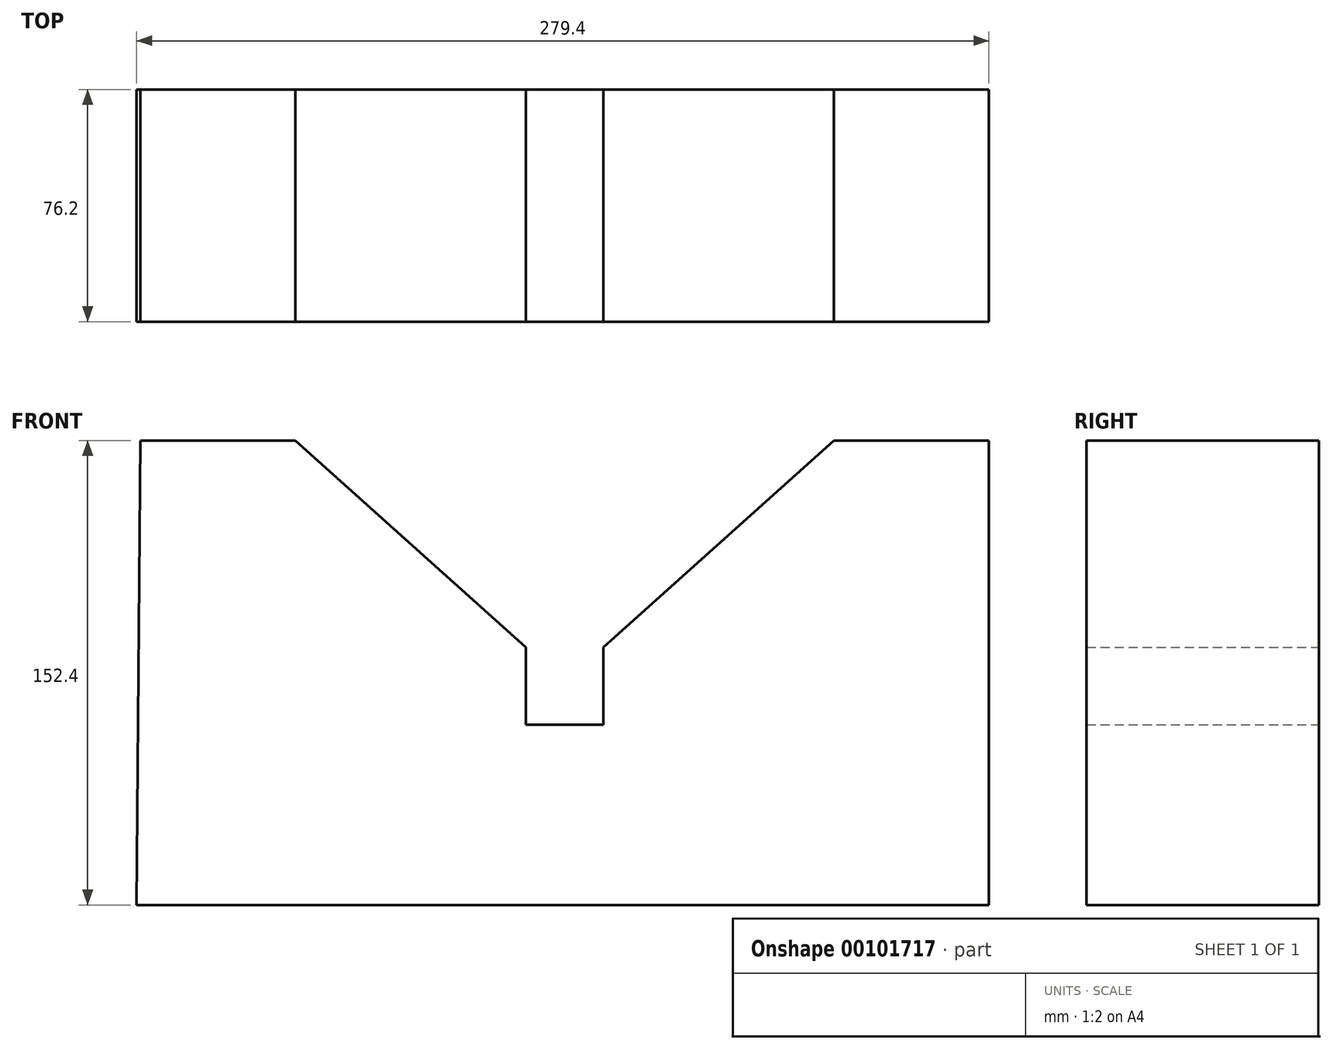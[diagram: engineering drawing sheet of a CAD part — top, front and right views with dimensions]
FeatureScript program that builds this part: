
annotation { "Feature Type Name" : "Feature", "Feature Type Description" : "" }
export const myFeature = defineFeature(function(context is Context, id is Id, definition is map)
    precondition{}
    {
        {
            var Q0;
            Q0=qCreatedBy(makeId("Front.planeOp"),FACE);
            var sketch = newSketch(context, id + "F0", { "sketchPlane" : qUnion([Q0])});
            skLineSegment(sketch, "E0", {"start": v(-116.18, 58.64) * mm, "end": v(-65.38, 58.64) * mm});
            skLineSegment(sketch, "E1", {"start": v(-65.38, 58.64) * mm, "end": v(10.19, -9.27) * mm});
            skLineSegment(sketch, "E2", {"start": v(10.19, -9.27) * mm, "end": v(10.19, -34.67) * mm});
            skLineSegment(sketch, "E3", {"start": v(10.19, -34.67) * mm, "end": v(35.59, -34.67) * mm});
            skLineSegment(sketch, "E4", {"start": v(35.59, -34.67) * mm, "end": v(35.59, -9.27) * mm});
            skLineSegment(sketch, "E5", {"start": v(35.59, -9.27) * mm, "end": v(111.15, 58.65) * mm});
            skLineSegment(sketch, "E6", {"start": v(111.15, 58.65) * mm, "end": v(161.95, 58.65) * mm});
            skLineSegment(sketch, "E7", {"start": v(161.95, 58.65) * mm, "end": v(161.95, -93.75) * mm});
            skLineSegment(sketch, "E8", {"start": v(161.95, -93.75) * mm, "end": v(-117.45, -93.75) * mm});
            skLineSegment(sketch, "E9", {"start": v(-117.45, -93.75) * mm, "end": v(-116.18, 58.64) * mm});
            skSolve(sketch);
        }
        {
            var Q0;
            Q0=makeQuery(id+"F0.imprint","IMPRINT",FACE,{"disambiguationData":[TD([[makeQuery(id+"F0.imprint","IMPRINT",EDGE,{"derivedFrom":sQuery(id+"F0.wireOp",EDGE,"E0")}),-1.0]])]});
            extrude(context, id + "F1", {"entities" : qUnion([Q0]), "depth" : 76.2 * mm});
        }
    });
